# Revit family: BX4-120
name_source: partatom
category: Lighting Fixtures
revit_build: Autodesk Revit 2014 (Build: 20130308_1515(x64)
units: mm (PartAtom-declared; Revit-internal decimal feet)

## types (5) — shared parameters
Apparent Load = 0 VA
Assembly Code = D5020220
Backbox = Steel - Hubbell
Baffle = Powdercoat - Hubbell - White
Color Filter = 16777215
Default Elevation = 48.000"
Description = 4in Line Voltage IC & Non-IC Downlights
Dimming Lamp Color Temperature Shift = <None>
Emit Shape Visible in Rendering = No
Emit from Circle Diameter = 4.500"
Glass = Hubbell - White Glass
Lamp = One PAR-16 or PAR-20/R-20 Lamp
Load Classification = Lighting
Manufacturer = Prescolite
Model = BX4-120
Power Factor = 1
Product Documentation Link = https://hubbellcdn.com
Product Page URL = https://www.hubbell.com
Tilt Angle = 90.00°
URL = https://www.hubbell.com
Voltage = 120 V

## per-type parameters (varying)
| type | Photometric Web File | Trims Option | Wattage Comments |
| BX4_120_TA120WW | bx4_120_ta120ww.ies | Baffle-120 : TA120WW | 50W |
| BX4_120_TA120WBF_50W_PAR20 | bx4_120_ta120wbf_50w_par20_nfl_ge.ies | Baffle-120 : TA120WBF | 50W |
| BX4_120_TA120C_50W_PAR20 | bx4_120_ta120c_50w_par20_nfl_ge.ies | Baffle-120 : TA120C | 50W |
| BX4_120_TA120BF_50W_PAR20 | bx4-120_ta120bf_50w_par20_nfl_ge.ies | Baffle-120 : TA120BF | 50W |
| BX4_120_TA120C_75W_PAR16 | bx4_120_ta120c_75w_par16_nfl_sylvania.ies | Baffle-120 : TA120C | 75 |

## geometry (parser evidence)
native form markers: Blend x3, Sweep x10
no freeform markers — native parametric forms only
